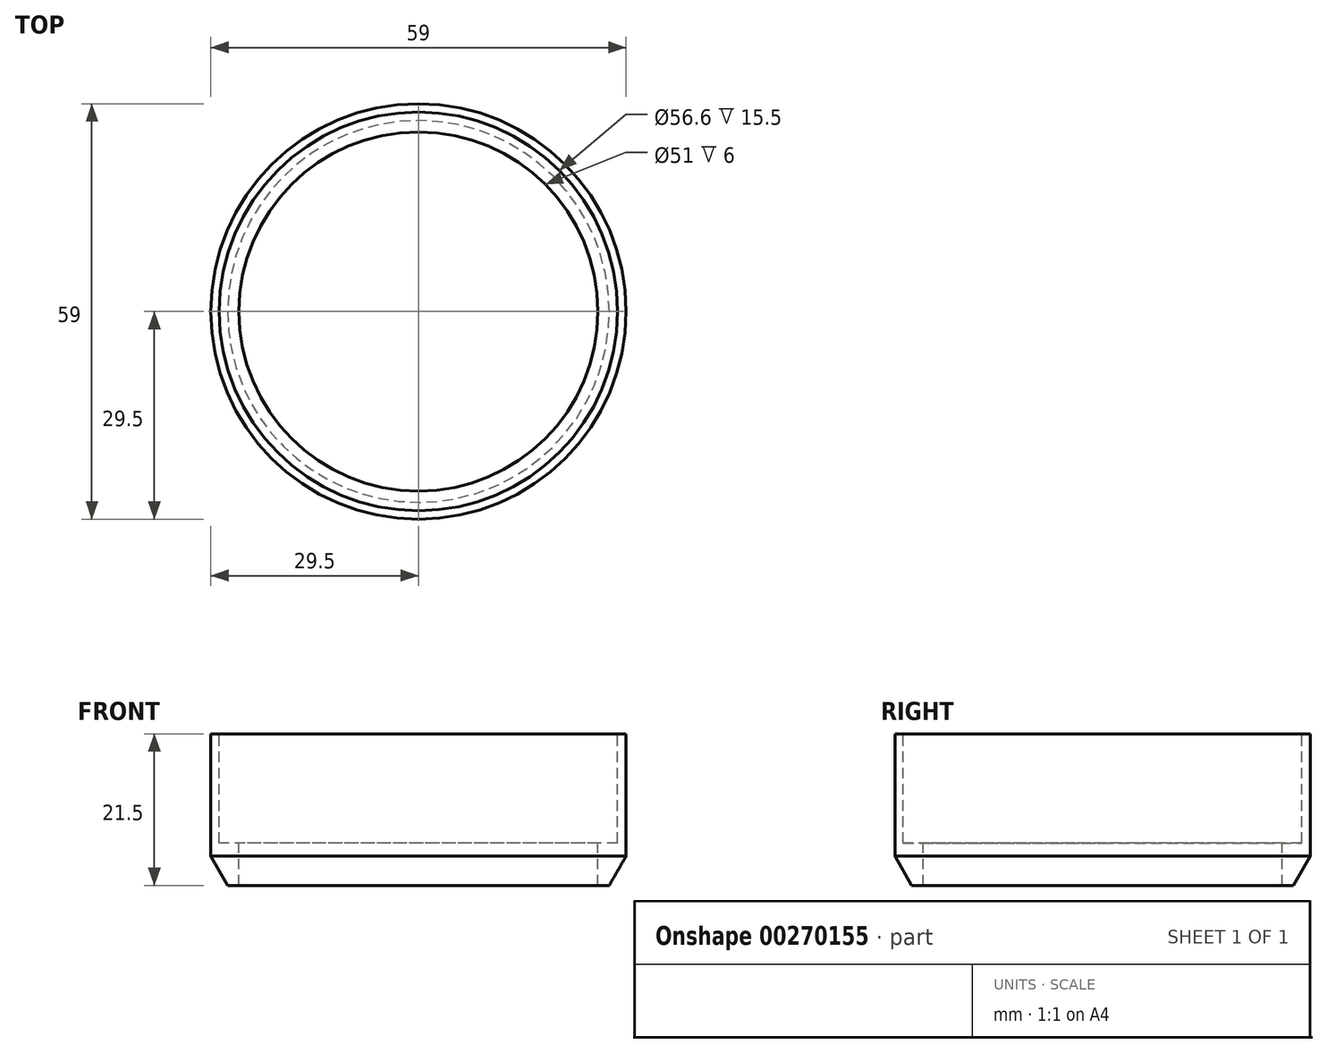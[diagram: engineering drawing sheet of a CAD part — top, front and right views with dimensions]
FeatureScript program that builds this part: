
annotation { "Feature Type Name" : "Feature", "Feature Type Description" : "" }
export const myFeature = defineFeature(function(context is Context, id is Id, definition is map)
    precondition{}
    {
        {
            var Q0;
            Q0=qCreatedBy(makeId("Front.planeOp"),FACE);
            var sketch = newSketch(context, id + "F0", { "sketchPlane" : qUnion([Q0])});
            skLineSegment(sketch, "E0", {"start": v(28.3, -13.87) * mm, "end": v(28.3, -29.37) * mm});
            skLineSegment(sketch, "E1", {"start": v(28.3, -29.37) * mm, "end": v(25.5, -29.37) * mm});
            skLineSegment(sketch, "E2", {"start": v(25.5, -29.37) * mm, "end": v(25.5, -35.37) * mm});
            skLineSegment(sketch, "E3", {"start": v(25.5, -35.37) * mm, "end": v(27.1, -35.37) * mm});
            skLineSegment(sketch, "E4", {"start": v(27.1, -35.37) * mm, "end": v(29.5, -31.21) * mm});
            skLineSegment(sketch, "E5", {"start": v(29.5, -31.21) * mm, "end": v(29.5, -13.87) * mm});
            skLineSegment(sketch, "E6", {"start": v(29.5, -13.87) * mm, "end": v(28.3, -13.87) * mm});
            skLineSegment(sketch, "E7", {"start": v(0, 24.42) * mm, "end": v(0, -13.18) * mm, "construction": true});
            skSolve(sketch);
        }
        {
            var Q0;
            Q0=makeQuery(id+"F0.imprint","IMPRINT",FACE,{"disambiguationData":[TD([[makeQuery(id+"F0.imprint","IMPRINT",EDGE,{"derivedFrom":sQuery(id+"F0.wireOp",EDGE,"E0")}),1.0]])]});
            var Q1;
            Q1=sQuery(id+"F0.wireOp",EDGE,"E7");
            revolve(context, id + "F1", {"entities" : qUnion([Q0]), "axis" : qUnion([Q1]), "revolveType" : RevolveType.FULL});
        }
    });
